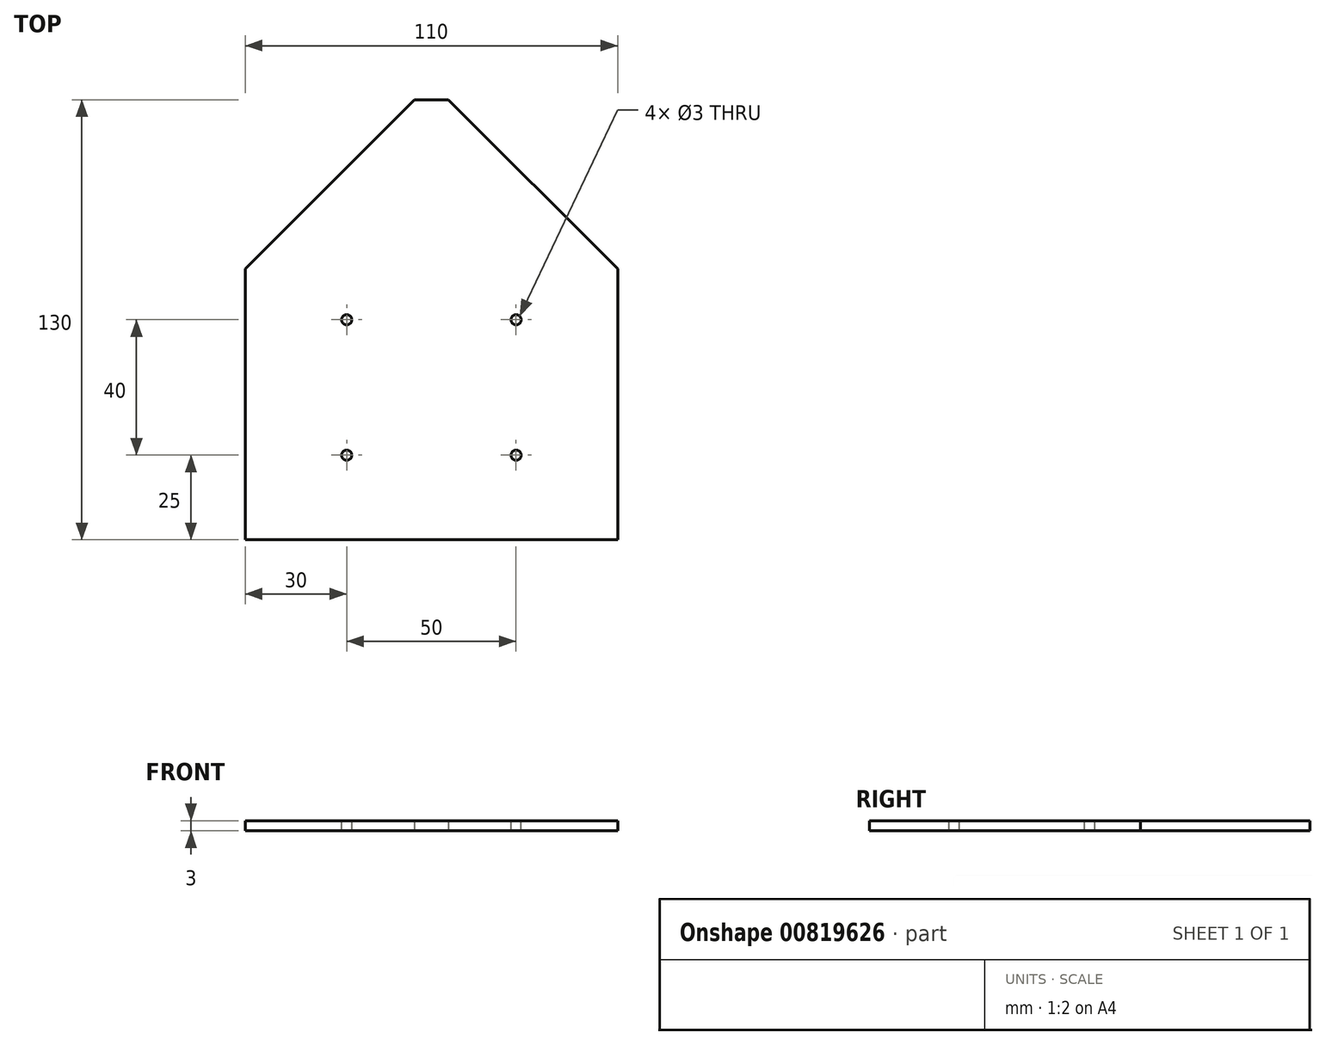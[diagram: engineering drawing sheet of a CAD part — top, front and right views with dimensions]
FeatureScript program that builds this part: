
annotation { "Feature Type Name" : "Feature", "Feature Type Description" : "" }
export const myFeature = defineFeature(function(context is Context, id is Id, definition is map)
    precondition{}
    {
        {
            var Q0;
            Q0=qCreatedBy(makeId("Top.planeOp"),FACE);
            var sketch = newSketch(context, id + "F0", { "sketchPlane" : qUnion([Q0])});
            skLineSegment(sketch, "E0.bottom", {"start": v(0, 0) * mm, "end": v(55, 0) * mm});
            skLineSegment(sketch, "E0.top", {"start": v(0, 130) * mm, "end": v(55, 130) * mm});
            skLineSegment(sketch, "E0.left", {"start": v(0, 0) * mm, "end": v(0, 130) * mm});
            skLineSegment(sketch, "E0.right", {"start": v(55, 0) * mm, "end": v(55, 130) * mm});
            skSolve(sketch);
        }
        {
            var Q0;
            Q0=makeQuery(id+"F0.imprint","IMPRINT",FACE,{"disambiguationData":[TD([[makeQuery(id+"F0.imprint","IMPRINT",EDGE,{"derivedFrom":sQuery(id+"F0.wireOp",EDGE,"E0.bottom")}),1.0]])]});
            extrude(context, id + "F1", {"entities" : qUnion([Q0]), "depth" : 3 * mm, "offsetDistance" : 25 * mm});
        }
        {
            var Q0;
            Q0=makeQuery(id+"F1.opExtrude","CAP_FACE",FACE,{"disambiguationData":[OSD([sQuery(id+"F0.wireOp",EDGE,"E0.bottom"),sQuery(id+"F0.wireOp",EDGE,"E0.top"),sQuery(id+"F0.wireOp",EDGE,"E0.left"),sQuery(id+"F0.wireOp",EDGE,"E0.right")])],"isStart":false});
            var sketch = newSketch(context, id + "F2", { "sketchPlane" : qUnion([Q0])});
            skLineSegment(sketch, "E1", {"start": v(25, 65) * mm, "end": v(25, 25) * mm});
            skSolve(sketch);
        }
        {
            var Q0;
            Q0=sQuery(id+"F2.wireOp",VERTEX,"E1.end");
            var Q1;
            Q1=sQuery(id+"F2.wireOp",VERTEX,"E1.start");
            var Q2;
            Q2=makeQuery(id+"F1.opExtrude","SWEPT_BODY",BODY,{"disambiguationData":[OSD([sQuery(id+"F0.wireOp",EDGE,"E0.bottom"),sQuery(id+"F0.wireOp",EDGE,"E0.top"),sQuery(id+"F0.wireOp",EDGE,"E0.left"),sQuery(id+"F0.wireOp",EDGE,"E0.right")])]});
            hole(context, id + "F3", {"style" : HoleStyle.SIMPLE, "endStyle" : HoleEndStyle.THROUGH, "holeDiameter" : 3 * mm, "majorDiameter" : 5 * mm, "isTappedThrough" : true, "tappedDepth" : 12 * mm, "tapClearance" : 3, "locations" : qUnion([Q0, Q1]), "scope" : qUnion([Q2])});
        }
        {
            var Q0;
            Q0=makeQuery(id+"F1.opExtrude","SWEPT_EDGE",EDGE,{"disambiguationData":[OSD([sQuery(id+"F0.wireOp",EDGE,"E0.top"),sQuery(id+"F0.wireOp",EDGE,"E0.right")])]});
            chamfer(context, id + "F4", {"entities" : qUnion([Q0]), "width" : 50 * mm, "tangentPropagation" : true});
        }
        {
            var Q0;
            Q0=makeQuery(id+"F1.opExtrude","SWEPT_BODY",BODY,{"disambiguationData":[OSD([sQuery(id+"F0.wireOp",EDGE,"E0.bottom"),sQuery(id+"F0.wireOp",EDGE,"E0.top"),sQuery(id+"F0.wireOp",EDGE,"E0.left"),sQuery(id+"F0.wireOp",EDGE,"E0.right")])]});
            var Q1;
            Q1=qCreatedBy(makeId("Right.planeOp"),FACE);
            mirror(context, id + "F5", {"operationType" : NewBodyOperationType.ADD, "entities" : qUnion([Q0]), "mirrorPlane" : qUnion([Q1])});
        }
    });
